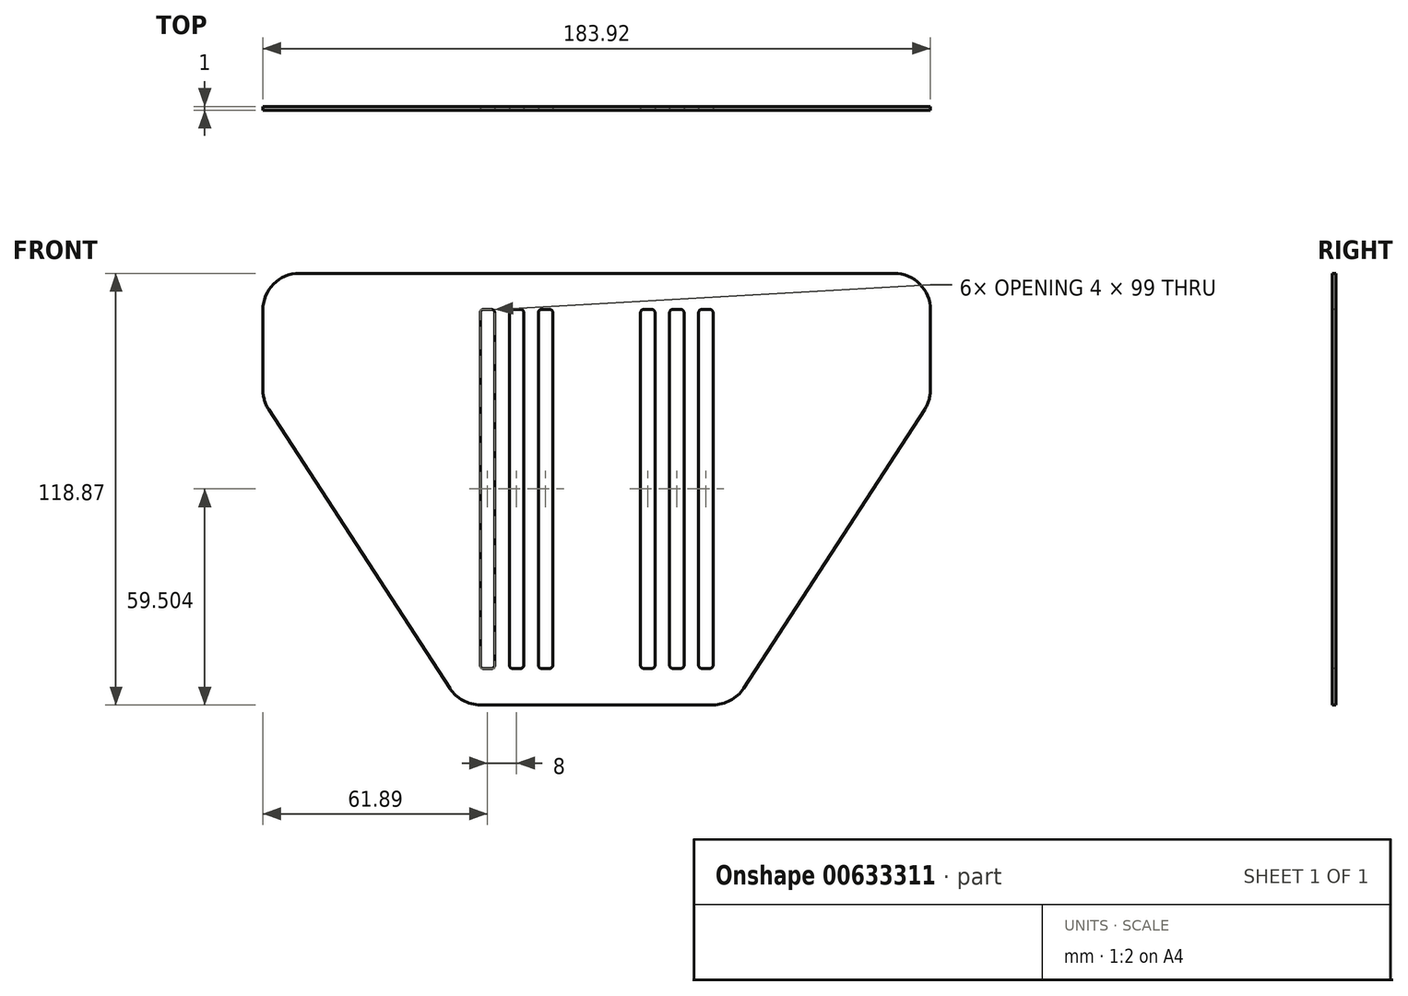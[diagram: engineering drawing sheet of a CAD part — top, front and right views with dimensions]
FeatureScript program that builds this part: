
annotation { "Feature Type Name" : "Feature", "Feature Type Description" : "" }
export const myFeature = defineFeature(function(context is Context, id is Id, definition is map)
    precondition{}
    {
        {
            var Q0;
            Q0=qCreatedBy(makeId("Front.planeOp"),FACE);
            var sketch = newSketch(context, id + "F0", { "sketchPlane" : qUnion([Q0])});
            skLineSegment(sketch, "E0", {"start": v(0, -57.5) * mm, "end": v(32.07, -57.5) * mm});
            skLineSegment(sketch, "E1", {"start": v(40.46, -52.95) * mm, "end": v(90.35, 23.88) * mm});
            skPoint(sketch, "E2.visualSharp", {"position": v(37.5, -57.5) * mm});
            skArc(sketch, "E2.filletArc", {"start": v(32.07, -57.5) * mm, "mid": v(36.84, -56.3) * mm, "end": v(40.46, -52.95) * mm});
            skLineSegment(sketch, "E3.MirrorCS", {"start": v(-40.46, -52.95) * mm, "end": v(-90.35, 23.88) * mm});
            skPoint(sketch, "E4.MirrorP", {"position": v(-37.5, -57.5) * mm});
            skLineSegment(sketch, "E5.MirrorCS", {"start": v(0, -57.5) * mm, "end": v(-32.07, -57.5) * mm});
            skArc(sketch, "E6.MirrorCS", {"start": v(-32.07, -57.5) * mm, "mid": v(-36.84, -56.3) * mm, "end": v(-40.46, -52.95) * mm});
            skLineSegment(sketch, "E7.top", {"start": v(-81.96, 61.36) * mm, "end": v(81.96, 61.36) * mm});
            skLineSegment(sketch, "E7.left", {"start": v(-91.96, 29.32) * mm, "end": v(-91.96, 51.36) * mm});
            skLineSegment(sketch, "E7.right", {"start": v(91.96, 29.32) * mm, "end": v(91.96, 51.36) * mm});
            skPoint(sketch, "E8.visualSharp", {"position": v(-91.96, 61.36) * mm});
            skArc(sketch, "E8.filletArc", {"start": v(-81.96, 61.36) * mm, "mid": v(-89.03, 58.43) * mm, "end": v(-91.96, 51.36) * mm});
            skPoint(sketch, "E9.visualSharp", {"position": v(91.96, 61.36) * mm});
            skArc(sketch, "E9.filletArc", {"start": v(91.96, 51.36) * mm, "mid": v(89.03, 58.43) * mm, "end": v(81.96, 61.36) * mm});
            skPoint(sketch, "E10.visualSharp", {"position": v(-91.96, 26.36) * mm});
            skArc(sketch, "E10.filletArc", {"start": v(-91.96, 29.32) * mm, "mid": v(-91.55, 26.48) * mm, "end": v(-90.35, 23.88) * mm});
            skPoint(sketch, "E11.visualSharp", {"position": v(91.96, 26.36) * mm});
            skArc(sketch, "E11.filletArc", {"start": v(90.35, 23.88) * mm, "mid": v(91.55, 26.48) * mm, "end": v(91.96, 29.32) * mm});
            skSolve(sketch);
        }
        {
            var Q0;
            Q0=makeQuery(id+"F0.imprint","IMPRINT",FACE,{"disambiguationData":[TD([[makeQuery(id+"F0.imprint","IMPRINT",EDGE,{"derivedFrom":sQuery(id+"F0.wireOp",EDGE,"E0")}),1.0]])]});
            extrude(context, id + "F1", {"entities" : qUnion([Q0]), "depth" : 1 * mm, "offsetDistance" : 25 * mm});
        }
        {
            var Q0;
            Q0=makeQuery(id+"F1.opExtrude","CAP_FACE",FACE,{"disambiguationData":[OSD([sQuery(id+"F0.wireOp",EDGE,"E0"),sQuery(id+"F0.wireOp",EDGE,"E1"),sQuery(id+"F0.wireOp",EDGE,"E2.filletArc"),sQuery(id+"F0.wireOp",EDGE,"E3.MirrorCS"),sQuery(id+"F0.wireOp",EDGE,"E5.MirrorCS"),sQuery(id+"F0.wireOp",EDGE,"E6.MirrorCS"),sQuery(id+"F0.wireOp",EDGE,"E7.top"),sQuery(id+"F0.wireOp",EDGE,"E7.left"),sQuery(id+"F0.wireOp",EDGE,"E7.right"),sQuery(id+"F0.wireOp",EDGE,"E8.filletArc"),sQuery(id+"F0.wireOp",EDGE,"E9.filletArc"),sQuery(id+"F0.wireOp",EDGE,"E10.filletArc"),sQuery(id+"F0.wireOp",EDGE,"E11.filletArc")])],"isStart":false});
            var sketch = newSketch(context, id + "F2", { "sketchPlane" : qUnion([Q0])});
            skLineSegment(sketch, "E12.bottom", {"start": v(-31.07, -47.5) * mm, "end": v(-29.07, -47.5) * mm});
            skLineSegment(sketch, "E12.top", {"start": v(-31.07, 51.5) * mm, "end": v(-29.07, 51.5) * mm});
            skLineSegment(sketch, "E12.left", {"start": v(-32.07, -46.5) * mm, "end": v(-32.07, 50.5) * mm});
            skLineSegment(sketch, "E12.right", {"start": v(-28.07, -46.5) * mm, "end": v(-28.07, 50.5) * mm});
            skLineSegment(sketch, "E13.bottom", {"start": v(-23.07, -47.5) * mm, "end": v(-21.07, -47.5) * mm});
            skLineSegment(sketch, "E13.top", {"start": v(-23.07, 51.5) * mm, "end": v(-21.07, 51.5) * mm});
            skLineSegment(sketch, "E13.left", {"start": v(-24.07, -46.5) * mm, "end": v(-24.07, 50.5) * mm});
            skLineSegment(sketch, "E13.right", {"start": v(-20.07, -46.5) * mm, "end": v(-20.07, 50.5) * mm});
            skLineSegment(sketch, "E14.bottom", {"start": v(-15.07, -47.5) * mm, "end": v(-13.07, -47.5) * mm});
            skLineSegment(sketch, "E14.top", {"start": v(-15.07, 51.5) * mm, "end": v(-13.07, 51.5) * mm});
            skLineSegment(sketch, "E14.left", {"start": v(-16.07, -46.5) * mm, "end": v(-16.07, 50.5) * mm});
            skLineSegment(sketch, "E14.right", {"start": v(-12.07, -46.5) * mm, "end": v(-12.07, 50.5) * mm});
            skPoint(sketch, "E15.visualSharp", {"position": v(-32.07, 51.5) * mm});
            skArc(sketch, "E15.filletArc", {"start": v(-31.07, 51.5) * mm, "mid": v(-31.78, 51.2) * mm, "end": v(-32.07, 50.5) * mm});
            skPoint(sketch, "E16.visualSharp", {"position": v(-28.07, 51.5) * mm});
            skArc(sketch, "E16.filletArc", {"start": v(-28.07, 50.5) * mm, "mid": v(-28.36, 51.2) * mm, "end": v(-29.07, 51.5) * mm});
            skPoint(sketch, "E17.visualSharp", {"position": v(-28.07, -47.5) * mm});
            skArc(sketch, "E17.filletArc", {"start": v(-29.07, -47.5) * mm, "mid": v(-28.36, -47.21) * mm, "end": v(-28.07, -46.5) * mm});
            skPoint(sketch, "E18.visualSharp", {"position": v(-32.07, -47.5) * mm});
            skArc(sketch, "E18.filletArc", {"start": v(-32.07, -46.5) * mm, "mid": v(-31.78, -47.21) * mm, "end": v(-31.07, -47.5) * mm});
            skPoint(sketch, "E19.visualSharp", {"position": v(-24.07, 51.5) * mm});
            skArc(sketch, "E19.filletArc", {"start": v(-23.07, 51.5) * mm, "mid": v(-23.78, 51.2) * mm, "end": v(-24.07, 50.5) * mm});
            skPoint(sketch, "E20.visualSharp", {"position": v(-20.07, 51.5) * mm});
            skArc(sketch, "E20.filletArc", {"start": v(-20.07, 50.5) * mm, "mid": v(-20.36, 51.2) * mm, "end": v(-21.07, 51.5) * mm});
            skPoint(sketch, "E21.visualSharp", {"position": v(-24.07, -47.5) * mm});
            skArc(sketch, "E21.filletArc", {"start": v(-24.07, -46.5) * mm, "mid": v(-23.78, -47.21) * mm, "end": v(-23.07, -47.5) * mm});
            skPoint(sketch, "E22.visualSharp", {"position": v(-20.07, -47.5) * mm});
            skArc(sketch, "E22.filletArc", {"start": v(-21.07, -47.5) * mm, "mid": v(-20.36, -47.21) * mm, "end": v(-20.07, -46.5) * mm});
            skPoint(sketch, "E23.visualSharp", {"position": v(-16.07, 51.5) * mm});
            skArc(sketch, "E23.filletArc", {"start": v(-15.07, 51.5) * mm, "mid": v(-15.78, 51.2) * mm, "end": v(-16.07, 50.5) * mm});
            skPoint(sketch, "E24.visualSharp", {"position": v(-12.07, 51.5) * mm});
            skArc(sketch, "E24.filletArc", {"start": v(-12.07, 50.5) * mm, "mid": v(-12.36, 51.2) * mm, "end": v(-13.07, 51.5) * mm});
            skPoint(sketch, "E25.visualSharp", {"position": v(-12.07, -47.5) * mm});
            skArc(sketch, "E25.filletArc", {"start": v(-13.07, -47.5) * mm, "mid": v(-12.36, -47.21) * mm, "end": v(-12.07, -46.5) * mm});
            skPoint(sketch, "E26.visualSharp", {"position": v(-16.07, -47.5) * mm});
            skArc(sketch, "E26.filletArc", {"start": v(-16.07, -46.5) * mm, "mid": v(-15.78, -47.21) * mm, "end": v(-15.07, -47.5) * mm});
            skArc(sketch, "E27.MirrorCS", {"start": v(16.07, -46.5) * mm, "mid": v(15.78, -47.21) * mm, "end": v(15.07, -47.5) * mm});
            skArc(sketch, "E28.MirrorCS", {"start": v(21.07, -47.5) * mm, "mid": v(20.36, -47.21) * mm, "end": v(20.07, -46.5) * mm});
            skArc(sketch, "E29.MirrorCS", {"start": v(29.07, -47.5) * mm, "mid": v(28.36, -47.21) * mm, "end": v(28.07, -46.5) * mm});
            skArc(sketch, "E30.MirrorCS", {"start": v(23.07, 51.5) * mm, "mid": v(23.78, 51.2) * mm, "end": v(24.07, 50.5) * mm});
            skArc(sketch, "E31.MirrorCS", {"start": v(32.07, -46.5) * mm, "mid": v(31.78, -47.21) * mm, "end": v(31.07, -47.5) * mm});
            skArc(sketch, "E32.MirrorCS", {"start": v(20.07, 50.5) * mm, "mid": v(20.36, 51.2) * mm, "end": v(21.07, 51.5) * mm});
            skArc(sketch, "E33.MirrorCS", {"start": v(15.07, 51.5) * mm, "mid": v(15.78, 51.2) * mm, "end": v(16.07, 50.5) * mm});
            skArc(sketch, "E34.MirrorCS", {"start": v(13.07, -47.5) * mm, "mid": v(12.36, -47.21) * mm, "end": v(12.07, -46.5) * mm});
            skLineSegment(sketch, "E35.MirrorCS", {"start": v(23.07, -47.5) * mm, "end": v(21.07, -47.5) * mm});
            skLineSegment(sketch, "E36.MirrorCS", {"start": v(15.07, -47.5) * mm, "end": v(13.07, -47.5) * mm});
            skLineSegment(sketch, "E37.MirrorCS", {"start": v(31.07, 51.5) * mm, "end": v(29.07, 51.5) * mm});
            skLineSegment(sketch, "E38.MirrorCS", {"start": v(31.07, -47.5) * mm, "end": v(29.07, -47.5) * mm});
            skLineSegment(sketch, "E39.MirrorCS", {"start": v(23.07, 51.5) * mm, "end": v(21.07, 51.5) * mm});
            skArc(sketch, "E40.MirrorCS", {"start": v(31.07, 51.5) * mm, "mid": v(31.78, 51.2) * mm, "end": v(32.07, 50.5) * mm});
            skArc(sketch, "E41.MirrorCS", {"start": v(28.07, 50.5) * mm, "mid": v(28.36, 51.2) * mm, "end": v(29.07, 51.5) * mm});
            skLineSegment(sketch, "E42.MirrorCS", {"start": v(15.07, 51.5) * mm, "end": v(13.07, 51.5) * mm});
            skArc(sketch, "E43.MirrorCS", {"start": v(12.07, 50.5) * mm, "mid": v(12.36, 51.2) * mm, "end": v(13.07, 51.5) * mm});
            skArc(sketch, "E44.MirrorCS", {"start": v(24.07, -46.5) * mm, "mid": v(23.78, -47.21) * mm, "end": v(23.07, -47.5) * mm});
            skPoint(sketch, "E45.MirrorP", {"position": v(28.07, -47.5) * mm});
            skPoint(sketch, "E46.MirrorP", {"position": v(16.07, 51.5) * mm});
            skPoint(sketch, "E47.MirrorP", {"position": v(32.07, 51.5) * mm});
            skPoint(sketch, "E48.MirrorP", {"position": v(12.07, -47.5) * mm});
            skPoint(sketch, "E49.MirrorP", {"position": v(20.07, -47.5) * mm});
            skPoint(sketch, "E50.MirrorP", {"position": v(32.07, -47.5) * mm});
            skPoint(sketch, "E51.MirrorP", {"position": v(16.07, -47.5) * mm});
            skPoint(sketch, "E52.MirrorP", {"position": v(12.07, 51.5) * mm});
            skPoint(sketch, "E53.MirrorP", {"position": v(28.07, 51.5) * mm});
            skLineSegment(sketch, "E54.MirrorCS", {"start": v(16.07, -46.5) * mm, "end": v(16.07, 50.5) * mm});
            skPoint(sketch, "E55.MirrorP", {"position": v(20.07, 51.5) * mm});
            skLineSegment(sketch, "E56.MirrorCS", {"start": v(12.07, -46.5) * mm, "end": v(12.07, 50.5) * mm});
            skLineSegment(sketch, "E57.MirrorCS", {"start": v(28.07, -46.5) * mm, "end": v(28.07, 50.5) * mm});
            skLineSegment(sketch, "E58.MirrorCS", {"start": v(32.07, -46.5) * mm, "end": v(32.07, 50.5) * mm});
            skLineSegment(sketch, "E59.MirrorCS", {"start": v(20.07, -46.5) * mm, "end": v(20.07, 50.5) * mm});
            skPoint(sketch, "E60.MirrorP", {"position": v(24.07, -47.5) * mm});
            skPoint(sketch, "E61.MirrorP", {"position": v(24.07, 51.5) * mm});
            skLineSegment(sketch, "E62.MirrorCS", {"start": v(24.07, -46.5) * mm, "end": v(24.07, 50.5) * mm});
            skSolve(sketch);
        }
        {
            var Q0;
            Q0 = qSketchRegion(id + "F2", true);
            extrude(context, id + "F3", {"entities" : qUnion([Q0]), "operationType" : NewBodyOperationType.REMOVE, "endBound" : BoundingType.THROUGH_ALL, "oppositeDirection" : true, "depth" : 25 * mm, "offsetDistance" : 25 * mm});
        }
    });
